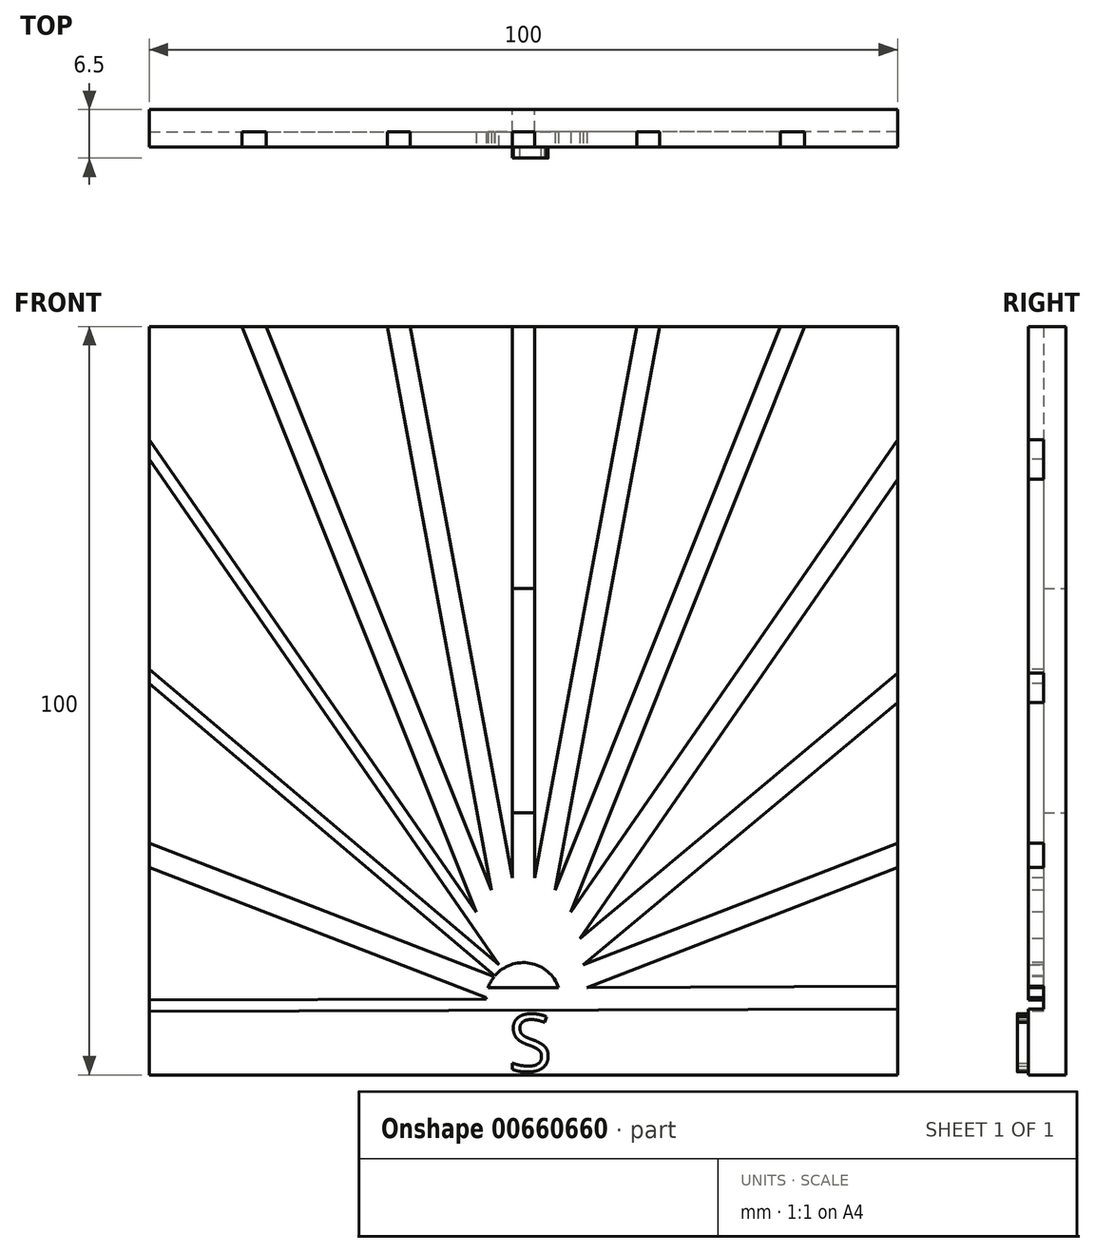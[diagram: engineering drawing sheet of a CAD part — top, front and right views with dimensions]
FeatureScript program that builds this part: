
annotation { "Feature Type Name" : "Feature", "Feature Type Description" : "" }
export const myFeature = defineFeature(function(context is Context, id is Id, definition is map)
    precondition{}
    {
        {
            var Q0;
            Q0=qCreatedBy(makeId("Front.planeOp"),FACE);
            var sketch = newSketch(context, id + "F0", { "sketchPlane" : qUnion([Q0])});
            skLineSegment(sketch, "E0.bottom", {"start": v(50, -50) * mm, "end": v(-50, -50) * mm});
            skLineSegment(sketch, "E0.top", {"start": v(50, 50) * mm, "end": v(-50, 50) * mm});
            skLineSegment(sketch, "E0.left", {"start": v(50, -50) * mm, "end": v(50, 50) * mm});
            skLineSegment(sketch, "E0.right", {"start": v(-50, -50) * mm, "end": v(-50, 50) * mm});
            skPoint(sketch, "E0.middle", {"position": v(0, 0) * mm});
            skLineSegment(sketch, "E1.bottom", {"start": v(1.5, -15) * mm, "end": v(-1.5, -15) * mm});
            skLineSegment(sketch, "E1.top", {"start": v(1.5, 15) * mm, "end": v(-1.5, 15) * mm});
            skLineSegment(sketch, "E1.left", {"start": v(1.5, -15) * mm, "end": v(1.5, 15) * mm});
            skLineSegment(sketch, "E1.right", {"start": v(-1.5, -15) * mm, "end": v(-1.5, 15) * mm});
            skSolve(sketch);
        }
        {
            var Q0;
            Q0=makeQuery(id+"F0.imprint","IMPRINT",FACE,{"disambiguationData":[TD([[makeQuery(id+"F0.imprint","IMPRINT",EDGE,{"derivedFrom":sQuery(id+"F0.wireOp",EDGE,"E0.bottom")}),-1.0]])]});
            extrude(context, id + "F1", {"entities" : qUnion([Q0]), "depth" : 5 * mm});
        }
        {
            var Q0;
            Q0=makeQuery(id+"F1.opExtrude","CAP_FACE",FACE,{"disambiguationData":[OSD([sQuery(id+"F0.wireOp",EDGE,"E0.bottom"),sQuery(id+"F0.wireOp",EDGE,"E0.top"),sQuery(id+"F0.wireOp",EDGE,"E0.left"),sQuery(id+"F0.wireOp",EDGE,"E0.right"),sQuery(id+"F0.wireOp",EDGE,"E1.bottom"),sQuery(id+"F0.wireOp",EDGE,"E1.top"),sQuery(id+"F0.wireOp",EDGE,"E1.left"),sQuery(id+"F0.wireOp",EDGE,"E1.right")])],"isStart":false});
            var sketch = newSketch(context, id + "F2", { "sketchPlane" : qUnion([Q0])});
            skPoint(sketch, "E2", {"position": v(0, -40) * mm});
            skLineSegment(sketch, "E3", {"start": v(-50, -40) * mm, "end": v(50, -40) * mm});
            skPoint(sketch, "E4", {"position": v(-50, -20.64) * mm});
            skLineSegment(sketch, "E5", {"start": v(0, -40) * mm, "end": v(-50, -20.64) * mm});
            skCircle(sketch, "E6", {"center": v(0, -40) * mm, "radius": 5 * mm});
            skPoint(sketch, "E7", {"position": v(-50, -19.03) * mm});
            skPoint(sketch, "E8", {"position": v(-50, -22.24) * mm});
            skLineSegment(sketch, "E9", {"start": v(-50, -22.24) * mm, "end": v(-4.99, -39.68) * mm});
            skLineSegment(sketch, "E10", {"start": v(-50, -19.03) * mm, "end": v(-3.9, -36.88) * mm});
            skSolve(sketch);
        }
        {
            var Q0;
            {var subQ5=sQuery(id+"F2.wireOp",EDGE,"E10");Q0=makeQuery(id+"F2.imprint","IMPRINT",FACE,{"disambiguationData":[TD([[makeQuery(id+"F2.imprint","IMPRINT",EDGE,{"derivedFrom":subQ5}),-1.0]])]});}
            var Q1;
            {var subQ5=sQuery(id+"F2.wireOp",EDGE,"E9");Q1=makeQuery(id+"F2.imprint","IMPRINT",FACE,{"disambiguationData":[TD([[makeQuery(id+"F2.imprint","IMPRINT",EDGE,{"derivedFrom":subQ5}),1.0]])]});}
            extrude(context, id + "F3", {"entities" : qUnion([Q0, Q1]), "operationType" : NewBodyOperationType.REMOVE, "oppositeDirection" : true, "depth" : 2 * mm});
        }
        {
            var Q0;
            Q0=makeQuery(id+"F1.opExtrude","CAP_FACE",FACE,{"disambiguationData":[OSD([sQuery(id+"F0.wireOp",EDGE,"E0.bottom"),sQuery(id+"F0.wireOp",EDGE,"E0.top"),sQuery(id+"F0.wireOp",EDGE,"E0.left"),sQuery(id+"F0.wireOp",EDGE,"E0.right"),sQuery(id+"F0.wireOp",EDGE,"E1.bottom"),sQuery(id+"F0.wireOp",EDGE,"E1.top"),sQuery(id+"F0.wireOp",EDGE,"E1.left"),sQuery(id+"F0.wireOp",EDGE,"E1.right")])],"isStart":false});
            var sketch = newSketch(context, id + "F4", { "sketchPlane" : qUnion([Q0])});
            skPoint(sketch, "E11", {"position": v(50, -41.82) * mm});
            skPoint(sketch, "E12", {"position": v(-50, 2.27) * mm});
            skPoint(sketch, "E13", {"position": v(0, -40) * mm});
            skCircle(sketch, "E14", {"center": v(0, -40) * mm, "radius": 5 * mm});
            skLineSegment(sketch, "E15", {"start": v(-50, 2.27) * mm, "end": v(0, -40) * mm});
            skLineSegment(sketch, "E16", {"start": v(0, -40) * mm, "end": v(-50, -39.68) * mm});
            skPoint(sketch, "E17", {"position": v(-50, 0.3) * mm});
            skPoint(sketch, "E18", {"position": v(-50, 4.23) * mm});
            skLineSegment(sketch, "E19", {"start": v(-50, 4.23) * mm, "end": v(-2.67, -35.78) * mm});
            skLineSegment(sketch, "E20", {"start": v(-50, 0.3) * mm, "end": v(-4.61, -38.07) * mm});
            skSolve(sketch);
        }
        {
            var Q0;
            {var subQ0=sQuery(id+"F4.wireOp",EDGE,"E19");Q0=makeQuery(id+"F4.imprint","IMPRINT",FACE,{"disambiguationData":[TD([[makeQuery(id+"F4.imprint","IMPRINT",EDGE,{"derivedFrom":subQ0}),-1.0]])]});}
            var Q1;
            {var subQ0=sQuery(id+"F4.wireOp",EDGE,"E14");var subQ1=sQuery(id+"F2.wireOp",EDGE,"E10");var subQ2=makeQuery(id+"F3.boolean.opBoolean","COPY",EDGE,{"derivedFrom":makeQuery(id+"F3.opExtrude","CAP_EDGE",EDGE,{"disambiguationData":[OSD([subQ1])],"isStart":true})});var subQ3=makeQuery(id+"F4.imprint","INTERSECT",VERTEX,{"derivedFrom":[subQ2,subQ0]});Q1=makeQuery(id+"F4.imprint","IMPRINT",FACE,{"disambiguationData":[TD([[makeQuery(id+"F4.imprint","IMPRINT",EDGE,{"disambiguationData":[TD([[subQ3,1.0]])],"derivedFrom":subQ0}),-1.0]])]});}
            extrude(context, id + "F5", {"entities" : qUnion([Q0, Q1]), "operationType" : NewBodyOperationType.REMOVE, "oppositeDirection" : true, "depth" : 2 * mm});
        }
        {
            var Q0;
            {var subQ0=sQuery(id+"F0.wireOp",EDGE,"E1.right");var subQ1=sQuery(id+"F0.wireOp",EDGE,"E1.left");var subQ2=sQuery(id+"F0.wireOp",EDGE,"E1.top");var subQ3=sQuery(id+"F0.wireOp",EDGE,"E1.bottom");var subQ4=sQuery(id+"F0.wireOp",EDGE,"E0.bottom");var subQ5=sQuery(id+"F0.wireOp",EDGE,"E0.right");var subQ6=sQuery(id+"F0.wireOp",EDGE,"E0.top");var subQ7=sQuery(id+"F0.wireOp",EDGE,"E0.left");Q0=makeQuery(id+"F5.boolean.opBoolean","SPLIT",FACE,{"disambiguationData":[TD([makeQuery(id+"F1.opExtrude","SWEPT_FACE",FACE,{"disambiguationData":[OSD([subQ4])]})])],"derivedFrom":makeQuery(id+"F1.opExtrude","CAP_FACE",FACE,{"disambiguationData":[OSD([subQ4,subQ6,subQ7,subQ5,subQ3,subQ2,subQ1,subQ0])],"isStart":false})});}
            var sketch = newSketch(context, id + "F6", { "sketchPlane" : qUnion([Q0])});
            skPoint(sketch, "E21", {"position": v(-50, 32.26) * mm});
            skPoint(sketch, "E22", {"position": v(0, -40) * mm});
            skCircle(sketch, "E23", {"center": v(0, -40) * mm, "radius": 5 * mm});
            skLineSegment(sketch, "E24", {"start": v(-50, 32.26) * mm, "end": v(0, -40) * mm});
            skLineSegment(sketch, "E25", {"start": v(0, -40) * mm, "end": v(-50, -40) * mm});
            skPoint(sketch, "E26", {"position": v(-50, 29.63) * mm});
            skPoint(sketch, "E27", {"position": v(-50, 34.9) * mm});
            skLineSegment(sketch, "E28", {"start": v(-50, 34.9) * mm, "end": v(-1.48, -35.22) * mm});
            skLineSegment(sketch, "E29", {"start": v(-50, 29.63) * mm, "end": v(-3.95, -36.93) * mm});
            skSolve(sketch);
        }
        {
            var Q0;
            {var subQ0=sQuery(id+"F6.wireOp",EDGE,"E28");Q0=makeQuery(id+"F6.imprint","IMPRINT",FACE,{"disambiguationData":[TD([[makeQuery(id+"F6.imprint","IMPRINT",EDGE,{"derivedFrom":subQ0}),-1.0]])]});}
            var Q1;
            {var subQ0=sQuery(id+"F6.wireOp",EDGE,"E23");var subQ1=sQuery(id+"F4.wireOp",EDGE,"E19");var subQ2=makeQuery(id+"F5.boolean.opBoolean","COPY",EDGE,{"derivedFrom":makeQuery(id+"F5.opExtrude","CAP_EDGE",EDGE,{"disambiguationData":[OSD([subQ1])],"isStart":true})});var subQ3=makeQuery(id+"F6.imprint","INTERSECT",VERTEX,{"derivedFrom":[subQ2,subQ0]});Q1=makeQuery(id+"F6.imprint","IMPRINT",FACE,{"disambiguationData":[TD([[makeQuery(id+"F6.imprint","IMPRINT",EDGE,{"disambiguationData":[TD([[subQ3,1.0]])],"derivedFrom":subQ0}),-1.0]])]});}
            var Q2;
            {var subQ6=sQuery(id+"F4.wireOp",EDGE,"E19");var subQ9=makeQuery(id+"F5.boolean.opBoolean","COPY",EDGE,{"derivedFrom":makeQuery(id+"F5.opExtrude","CAP_EDGE",EDGE,{"disambiguationData":[OSD([subQ6])],"isStart":true})});var subQ11=sQuery(id+"F6.wireOp",EDGE,"E29");var subQ12=makeQuery(id+"F6.imprint","INTERSECT",VERTEX,{"derivedFrom":[subQ9,subQ11]});Q2=makeQuery(id+"F6.imprint","IMPRINT",FACE,{"disambiguationData":[TD([[makeQuery(id+"F6.imprint","IMPRINT",EDGE,{"disambiguationData":[TD([[subQ12,-1.0]])],"derivedFrom":subQ9}),1.0]])]});}
            extrude(context, id + "F7", {"entities" : qUnion([Q0, Q1, Q2]), "operationType" : NewBodyOperationType.REMOVE, "oppositeDirection" : true, "depth" : 2 * mm});
        }
        {
            var Q0;
            {var subQ0=sQuery(id+"F0.wireOp",EDGE,"E1.right");var subQ2=sQuery(id+"F0.wireOp",EDGE,"E1.left");var subQ5=sQuery(id+"F0.wireOp",EDGE,"E1.top");var subQ7=sQuery(id+"F0.wireOp",EDGE,"E1.bottom");var subQ9=sQuery(id+"F0.wireOp",EDGE,"E0.bottom");var subQ10=makeQuery(id+"F1.opExtrude","SWEPT_FACE",FACE,{"disambiguationData":[OSD([subQ9])]});var subQ12=sQuery(id+"F0.wireOp",EDGE,"E0.right");var subQ14=sQuery(id+"F0.wireOp",EDGE,"E0.top");var subQ16=sQuery(id+"F0.wireOp",EDGE,"E0.left");Q0=makeQuery(id+"F7.boolean.opBoolean","SPLIT",FACE,{"disambiguationData":[TD([subQ10])],"derivedFrom":makeQuery(id+"F5.boolean.opBoolean","SPLIT",FACE,{"disambiguationData":[TD([subQ10])],"derivedFrom":makeQuery(id+"F1.opExtrude","CAP_FACE",FACE,{"disambiguationData":[OSD([subQ9,subQ14,subQ16,subQ12,subQ7,subQ5,subQ2,subQ0])],"isStart":false})})});}
            var sketch = newSketch(context, id + "F8", { "sketchPlane" : qUnion([Q0])});
            skPoint(sketch, "E30", {"position": v(0, -40) * mm});
            skPoint(sketch, "E31", {"position": v(-35.96, 50) * mm});
            skLineSegment(sketch, "E32", {"start": v(-35.96, 50) * mm, "end": v(0, -40) * mm});
            skLineSegment(sketch, "E33", {"start": v(0, -40) * mm, "end": v(-50, -40) * mm});
            skPoint(sketch, "E34", {"position": v(-37.58, 50) * mm});
            skPoint(sketch, "E35", {"position": v(-34.35, 50) * mm});
            skCircle(sketch, "E36", {"center": v(0, -40) * mm, "radius": 5 * mm});
            skLineSegment(sketch, "E37", {"start": v(-34.35, 50) * mm, "end": v(-0.38, -35.01) * mm});
            skLineSegment(sketch, "E38", {"start": v(-37.58, 50) * mm, "end": v(-3.16, -36.13) * mm});
            skSolve(sketch);
        }
        {
            var Q0;
            {var subQ0=sQuery(id+"F8.wireOp",EDGE,"E32");var subQ1=makeQuery(id+"F1.opExtrude","CAP_EDGE",EDGE,{"disambiguationData":[OSD([sQuery(id+"F0.wireOp",EDGE,"E0.top")])],"isStart":false});var subQ2=makeQuery(id+"F8.imprint","INTERSECT",VERTEX,{"derivedFrom":[subQ1,subQ0]});Q0=makeQuery(id+"F8.imprint","IMPRINT",FACE,{"disambiguationData":[TD([[makeQuery(id+"F8.imprint","IMPRINT",EDGE,{"disambiguationData":[TD([[subQ2,-1.0]])],"derivedFrom":subQ0}),-1.0]])]});}
            var Q1;
            {var subQ5=sQuery(id+"F8.wireOp",EDGE,"E37");Q1=makeQuery(id+"F8.imprint","IMPRINT",FACE,{"disambiguationData":[TD([[makeQuery(id+"F8.imprint","IMPRINT",EDGE,{"derivedFrom":subQ5}),-1.0]])]});}
            extrude(context, id + "F9", {"entities" : qUnion([Q0, Q1]), "operationType" : NewBodyOperationType.REMOVE, "oppositeDirection" : true, "depth" : 2 * mm});
        }
        {
            var Q0;
            {var subQ0=sQuery(id+"F0.wireOp",EDGE,"E1.right");var subQ2=sQuery(id+"F0.wireOp",EDGE,"E1.left");var subQ5=sQuery(id+"F0.wireOp",EDGE,"E1.top");var subQ8=sQuery(id+"F0.wireOp",EDGE,"E1.bottom");var subQ10=sQuery(id+"F0.wireOp",EDGE,"E0.bottom");var subQ11=makeQuery(id+"F1.opExtrude","SWEPT_FACE",FACE,{"disambiguationData":[OSD([subQ10])]});var subQ13=sQuery(id+"F0.wireOp",EDGE,"E0.right");var subQ15=sQuery(id+"F0.wireOp",EDGE,"E0.top");var subQ17=sQuery(id+"F0.wireOp",EDGE,"E0.left");Q0=makeQuery(id+"F9.boolean.opBoolean","SPLIT",FACE,{"disambiguationData":[TD([subQ11])],"derivedFrom":makeQuery(id+"F7.boolean.opBoolean","SPLIT",FACE,{"disambiguationData":[TD([subQ11])],"derivedFrom":makeQuery(id+"F5.boolean.opBoolean","SPLIT",FACE,{"disambiguationData":[TD([subQ11])],"derivedFrom":makeQuery(id+"F1.opExtrude","CAP_FACE",FACE,{"disambiguationData":[OSD([subQ10,subQ15,subQ17,subQ13,subQ8,subQ5,subQ2,subQ0])],"isStart":false})})})});}
            var sketch = newSketch(context, id + "F10", { "sketchPlane" : qUnion([Q0])});
            skPoint(sketch, "E39", {"position": v(0, -40) * mm});
            skPoint(sketch, "E40", {"position": v(-16.68, 50) * mm});
            skPoint(sketch, "E41", {"position": v(-15.15, 50) * mm});
            skPoint(sketch, "E42", {"position": v(-18.2, 50) * mm});
            skCircle(sketch, "E43", {"center": v(0, -40) * mm, "radius": 5 * mm});
            skLineSegment(sketch, "E44", {"start": v(-16.68, 50) * mm, "end": v(0, -40) * mm});
            skLineSegment(sketch, "E45", {"start": v(0, -40) * mm, "end": v(-50, -40) * mm});
            skLineSegment(sketch, "E46", {"start": v(-18.2, 50) * mm, "end": v(-2.34, -35.58) * mm});
            skLineSegment(sketch, "E47", {"start": v(-15.15, 50) * mm, "end": v(0.6, -35.04) * mm});
            skSolve(sketch);
        }
        {
            var Q0;
            {var subQ3=sQuery(id+"F8.wireOp",EDGE,"E37");var subQ6=makeQuery(id+"F9.boolean.opBoolean","COPY",EDGE,{"derivedFrom":makeQuery(id+"F9.opExtrude","CAP_EDGE",EDGE,{"disambiguationData":[OSD([subQ3])],"isStart":true})});var subQ8=sQuery(id+"F10.wireOp",EDGE,"E46");var subQ10=makeQuery(id+"F10.imprint","INTERSECT",VERTEX,{"derivedFrom":[subQ6,subQ8]});Q0=makeQuery(id+"F10.imprint","IMPRINT",FACE,{"disambiguationData":[TD([[makeQuery(id+"F10.imprint","IMPRINT",EDGE,{"disambiguationData":[TD([[subQ10,-1.0]])],"derivedFrom":subQ6}),1.0]])]});}
            var Q1;
            {var subQ6=sQuery(id+"F10.wireOp",EDGE,"E47");Q1=makeQuery(id+"F10.imprint","IMPRINT",FACE,{"disambiguationData":[TD([[makeQuery(id+"F10.imprint","IMPRINT",EDGE,{"derivedFrom":subQ6}),-1.0]])]});}
            extrude(context, id + "F11", {"entities" : qUnion([Q0, Q1]), "operationType" : NewBodyOperationType.REMOVE, "oppositeDirection" : true, "depth" : 2 * mm});
        }
        {
            var Q0;
            {var subQ0=sQuery(id+"F0.wireOp",EDGE,"E1.right");var subQ2=sQuery(id+"F0.wireOp",EDGE,"E1.left");var subQ5=sQuery(id+"F0.wireOp",EDGE,"E1.top");var subQ8=sQuery(id+"F0.wireOp",EDGE,"E1.bottom");var subQ10=sQuery(id+"F0.wireOp",EDGE,"E0.bottom");var subQ11=makeQuery(id+"F1.opExtrude","SWEPT_FACE",FACE,{"disambiguationData":[OSD([subQ10])]});var subQ13=sQuery(id+"F0.wireOp",EDGE,"E0.right");var subQ15=sQuery(id+"F0.wireOp",EDGE,"E0.top");var subQ17=sQuery(id+"F0.wireOp",EDGE,"E0.left");Q0=makeQuery(id+"F11.boolean.opBoolean","SPLIT",FACE,{"disambiguationData":[TD([subQ11])],"derivedFrom":makeQuery(id+"F9.boolean.opBoolean","SPLIT",FACE,{"disambiguationData":[TD([subQ11])],"derivedFrom":makeQuery(id+"F7.boolean.opBoolean","SPLIT",FACE,{"disambiguationData":[TD([subQ11])],"derivedFrom":makeQuery(id+"F5.boolean.opBoolean","SPLIT",FACE,{"disambiguationData":[TD([subQ11])],"derivedFrom":makeQuery(id+"F1.opExtrude","CAP_FACE",FACE,{"disambiguationData":[OSD([subQ10,subQ15,subQ17,subQ13,subQ8,subQ5,subQ2,subQ0])],"isStart":false})})})})});}
            var sketch = newSketch(context, id + "F12", { "sketchPlane" : qUnion([Q0])});
            skPoint(sketch, "E48", {"position": v(0, -40) * mm});
            skPoint(sketch, "E49", {"position": v(0, 50) * mm});
            skLineSegment(sketch, "E50", {"start": v(0, 50) * mm, "end": v(0, -40) * mm});
            skPoint(sketch, "E51", {"position": v(-1.5, 50) * mm});
            skPoint(sketch, "E52", {"position": v(1.5, 50) * mm});
            skCircle(sketch, "E53", {"center": v(0, -40) * mm, "radius": 5 * mm});
            skLineSegment(sketch, "E54", {"start": v(-1.5, 50) * mm, "end": v(-1.5, -35.23) * mm});
            skLineSegment(sketch, "E55", {"start": v(1.5, 50) * mm, "end": v(1.5, -35.23) * mm});
            skSolve(sketch);
        }
        {
            var Q0;
            {var subQ0=sQuery(id+"F12.wireOp",EDGE,"E50");var subQ1=sQuery(id+"F0.wireOp",EDGE,"E1.top");var subQ9=makeQuery(id+"F1.opExtrude","CAP_EDGE",EDGE,{"disambiguationData":[OSD([subQ1])],"isStart":false});var subQ10=makeQuery(id+"F12.imprint","INTERSECT",VERTEX,{"derivedFrom":[subQ9,subQ0]});Q0=makeQuery(id+"F12.imprint","IMPRINT",FACE,{"disambiguationData":[TD([[makeQuery(id+"F12.imprint","IMPRINT",EDGE,{"disambiguationData":[TD([[subQ10,-1.0]])],"derivedFrom":subQ9}),-1.0]])]});}
            var Q1;
            {var subQ0=sQuery(id+"F12.wireOp",EDGE,"E50");var subQ1=sQuery(id+"F0.wireOp",EDGE,"E1.top");var subQ9=makeQuery(id+"F1.opExtrude","CAP_EDGE",EDGE,{"disambiguationData":[OSD([subQ1])],"isStart":false});var subQ10=makeQuery(id+"F12.imprint","INTERSECT",VERTEX,{"derivedFrom":[subQ9,subQ0]});Q1=makeQuery(id+"F12.imprint","IMPRINT",FACE,{"disambiguationData":[TD([[makeQuery(id+"F12.imprint","IMPRINT",EDGE,{"disambiguationData":[TD([[subQ10,1.0]])],"derivedFrom":subQ9}),-1.0]])]});}
            var Q2;
            {var subQ0=sQuery(id+"F12.wireOp",EDGE,"E50");var subQ1=makeQuery(id+"F1.opExtrude","CAP_EDGE",EDGE,{"disambiguationData":[OSD([sQuery(id+"F0.wireOp",EDGE,"E1.bottom")])],"isStart":false});var subQ2=makeQuery(id+"F12.imprint","INTERSECT",VERTEX,{"derivedFrom":[subQ1,subQ0]});Q2=makeQuery(id+"F12.imprint","IMPRINT",FACE,{"disambiguationData":[TD([[makeQuery(id+"F12.imprint","IMPRINT",EDGE,{"disambiguationData":[TD([[subQ2,-1.0]])],"derivedFrom":subQ0}),-1.0]])]});}
            var Q3;
            {var subQ3=makeQuery(id+"F1.opExtrude","CAP_EDGE",EDGE,{"disambiguationData":[OSD([sQuery(id+"F0.wireOp",EDGE,"E1.bottom")])],"isStart":false});var subQ7=sQuery(id+"F12.wireOp",EDGE,"E50");var subQ9=makeQuery(id+"F12.imprint","INTERSECT",VERTEX,{"derivedFrom":[subQ3,subQ7]});Q3=makeQuery(id+"F12.imprint","IMPRINT",FACE,{"disambiguationData":[TD([[makeQuery(id+"F12.imprint","IMPRINT",EDGE,{"disambiguationData":[TD([[subQ9,-1.0]])],"derivedFrom":subQ7}),1.0]])]});}
            var Q4;
            {var subQ0=sQuery(id+"F12.wireOp",EDGE,"E53");var subQ1=sQuery(id+"F12.wireOp",EDGE,"E50");var subQ2=makeQuery(id+"F12.imprint","INTERSECT",VERTEX,{"derivedFrom":[subQ1,subQ0]});Q4=makeQuery(id+"F12.imprint","IMPRINT",FACE,{"disambiguationData":[TD([[makeQuery(id+"F12.imprint","IMPRINT",EDGE,{"disambiguationData":[TD([[subQ2,1.0]])],"derivedFrom":subQ1}),-1.0]])]});}
            extrude(context, id + "F13", {"entities" : qUnion([Q0, Q1, Q2, Q3, Q4]), "operationType" : NewBodyOperationType.REMOVE, "oppositeDirection" : true, "depth" : 2 * mm});
        }
        {
            var Q0;
            {var subQ0=sQuery(id+"F0.wireOp",EDGE,"E1.left");var subQ3=sQuery(id+"F0.wireOp",EDGE,"E1.top");var subQ7=sQuery(id+"F0.wireOp",EDGE,"E1.bottom");var subQ9=sQuery(id+"F0.wireOp",EDGE,"E0.bottom");var subQ10=makeQuery(id+"F1.opExtrude","SWEPT_FACE",FACE,{"disambiguationData":[OSD([subQ9])]});var subQ12=sQuery(id+"F0.wireOp",EDGE,"E0.right");var subQ14=sQuery(id+"F0.wireOp",EDGE,"E0.top");var subQ20=sQuery(id+"F0.wireOp",EDGE,"E0.left");var subQ24=sQuery(id+"F0.wireOp",EDGE,"E1.right");var subQ25=makeQuery(id+"F1.opExtrude","CAP_FACE",FACE,{"disambiguationData":[OSD([subQ9,subQ14,subQ20,subQ12,subQ7,subQ3,subQ0,subQ24])],"isStart":false});Q0=makeQuery(id+"F13.boolean.opBoolean","SPLIT",FACE,{"disambiguationData":[TD([subQ10])],"derivedFrom":makeQuery(id+"F11.boolean.opBoolean","SPLIT",FACE,{"disambiguationData":[TD([subQ10])],"derivedFrom":makeQuery(id+"F9.boolean.opBoolean","SPLIT",FACE,{"disambiguationData":[TD([subQ10])],"derivedFrom":makeQuery(id+"F7.boolean.opBoolean","SPLIT",FACE,{"disambiguationData":[TD([subQ10])],"derivedFrom":makeQuery(id+"F5.boolean.opBoolean","SPLIT",FACE,{"disambiguationData":[TD([subQ10])],"derivedFrom":subQ25})})})})});}
            var sketch = newSketch(context, id + "F14", { "sketchPlane" : qUnion([Q0])});
            skPoint(sketch, "E56", {"position": v(16.68, 50) * mm});
            skPoint(sketch, "E57", {"position": v(0, -40) * mm});
            skCircle(sketch, "E58", {"center": v(0, -40) * mm, "radius": 5 * mm});
            skLineSegment(sketch, "E59", {"start": v(16.68, 50) * mm, "end": v(0, -40) * mm});
            skLineSegment(sketch, "E60", {"start": v(0, -40) * mm, "end": v(50, -40) * mm});
            skPoint(sketch, "E61", {"position": v(15.15, 50) * mm});
            skPoint(sketch, "E62", {"position": v(18.2, 50) * mm});
            skLineSegment(sketch, "E63", {"start": v(18.2, 50) * mm, "end": v(2.34, -35.58) * mm});
            skLineSegment(sketch, "E64", {"start": v(15.15, 50) * mm, "end": v(-0.6, -35.04) * mm});
            skSolve(sketch);
        }
        {
            var Q0;
            {var subQ7=sQuery(id+"F14.wireOp",EDGE,"E63");Q0=makeQuery(id+"F14.imprint","IMPRINT",FACE,{"disambiguationData":[TD([[makeQuery(id+"F14.imprint","IMPRINT",EDGE,{"derivedFrom":subQ7}),-1.0]])]});}
            var Q1;
            {var subQ6=sQuery(id+"F12.wireOp",EDGE,"E55");var subQ12=makeQuery(id+"F13.boolean.opBoolean","COPY",EDGE,{"derivedFrom":makeQuery(id+"F13.opExtrude","CAP_EDGE",EDGE,{"disambiguationData":[OSD([subQ6]),TDD([makeQuery(id+"F12.imprint","IMPRINT",EDGE,{"disambiguationData":[TD([[makeQuery(id+"F12.imprint","INTERSECT",VERTEX,{"derivedFrom":[sQuery(id+"F12.wireOp",EDGE,"E53"),subQ6]}),1.0]])],"derivedFrom":subQ6})])],"isStart":true})});var subQ14=sQuery(id+"F14.wireOp",EDGE,"U3o0jyPI-7KGk-aDnc-HRvP-a0akFUZvhtuf");var subQ16=makeQuery(id+"F14.imprint","INTERSECT",VERTEX,{"derivedFrom":[subQ12,subQ14]});Q1=makeQuery(id+"F14.imprint","IMPRINT",FACE,{"disambiguationData":[TD([[makeQuery(id+"F14.imprint","IMPRINT",EDGE,{"disambiguationData":[TD([[subQ16,-1.0]])],"derivedFrom":subQ12}),1.0]])]});}
            var Q2;
            {var subQ1=sQuery(id+"F0.wireOp",EDGE,"E0.left");var subQ2=makeQuery(id+"F1.opExtrude","SWEPT_FACE",FACE,{"disambiguationData":[OSD([subQ1])]});var subQ3=sQuery(id+"F0.wireOp",EDGE,"E1.left");var subQ4=sQuery(id+"F0.wireOp",EDGE,"E0.top");var subQ6=sQuery(id+"F12.wireOp",EDGE,"E55");var subQ7=sQuery(id+"F0.wireOp",EDGE,"E1.bottom");var subQ8=makeQuery(id+"F12.imprint","IMPRINT",EDGE,{"disambiguationData":[TD([[makeQuery(id+"F12.imprint","INTERSECT",VERTEX,{"derivedFrom":[makeQuery(id+"F1.opExtrude","CAP_EDGE",EDGE,{"disambiguationData":[OSD([subQ7])],"isStart":false}),subQ6]}),-1.0],[makeQuery(id+"F12.imprint","INTERSECT",VERTEX,{"derivedFrom":[sQuery(id+"F12.wireOp",EDGE,"E53"),subQ6]}),1.0]])],"derivedFrom":subQ6});var subQ9=sQuery(id+"F0.wireOp",EDGE,"E1.top");var subQ11=makeQuery(id+"F11.boolean.opBoolean","SPLIT",EDGE,{"disambiguationData":[TD([subQ2])],"derivedFrom":makeQuery(id+"F9.boolean.opBoolean","SPLIT",EDGE,{"disambiguationData":[TD([subQ2])],"derivedFrom":makeQuery(id+"F1.opExtrude","CAP_EDGE",EDGE,{"disambiguationData":[OSD([subQ4])],"isStart":false})})});var subQ12=makeQuery(id+"F12.imprint","IMPRINT",EDGE,{"disambiguationData":[TD([[makeQuery(id+"F12.imprint","INTERSECT",VERTEX,{"derivedFrom":[makeQuery(id+"F1.opExtrude","CAP_EDGE",EDGE,{"disambiguationData":[OSD([subQ9])],"isStart":false}),subQ6]}),1.0],[makeQuery(id+"F12.imprint","INTERSECT",VERTEX,{"derivedFrom":[subQ11,subQ6]}),-1.0]])],"derivedFrom":subQ6});var subQ15=makeQuery(id+"F13.boolean.opBoolean","MERGE",EDGE,{"derivedFrom":[makeQuery(id+"F1.opExtrude","CAP_EDGE",EDGE,{"disambiguationData":[OSD([subQ3])],"isStart":false}),makeQuery(id+"F13.opExtrude","CAP_EDGE",EDGE,{"disambiguationData":[OSD([subQ6]),TDD([subQ12])],"isStart":true}),makeQuery(id+"F13.opExtrude","CAP_EDGE",EDGE,{"disambiguationData":[OSD([subQ6]),TDD([subQ8])],"isStart":true})]});var subQ17=sQuery(id+"F14.wireOp",EDGE,"E64");var subQ18=makeQuery(id+"F14.imprint","INTERSECT",VERTEX,{"derivedFrom":[subQ15,subQ17]});Q2=makeQuery(id+"F14.imprint","IMPRINT",FACE,{"disambiguationData":[TD([[makeQuery(id+"F14.imprint","IMPRINT",EDGE,{"disambiguationData":[TD([[subQ18,1.0]])],"derivedFrom":subQ15}),-1.0]])]});}
            extrude(context, id + "F15", {"entities" : qUnion([Q0, Q1, Q2]), "operationType" : NewBodyOperationType.REMOVE, "oppositeDirection" : true, "depth" : 2 * mm});
        }
        {
            var Q0;
            {var subQ4=sQuery(id+"F0.wireOp",EDGE,"E0.bottom");var subQ5=makeQuery(id+"F1.opExtrude","SWEPT_FACE",FACE,{"disambiguationData":[OSD([subQ4])]});var subQ8=sQuery(id+"F0.wireOp",EDGE,"E0.right");var subQ10=sQuery(id+"F0.wireOp",EDGE,"E0.top");var subQ17=sQuery(id+"F0.wireOp",EDGE,"E0.left");var subQ19=sQuery(id+"F0.wireOp",EDGE,"E1.left");var subQ21=sQuery(id+"F0.wireOp",EDGE,"E1.top");var subQ23=sQuery(id+"F0.wireOp",EDGE,"E1.bottom");var subQ25=sQuery(id+"F0.wireOp",EDGE,"E1.right");var subQ26=makeQuery(id+"F1.opExtrude","CAP_FACE",FACE,{"disambiguationData":[OSD([subQ4,subQ10,subQ17,subQ8,subQ23,subQ21,subQ19,subQ25])],"isStart":false});Q0=makeQuery(id+"F15.boolean.opBoolean","SPLIT",FACE,{"disambiguationData":[TD([subQ5])],"derivedFrom":makeQuery(id+"F13.boolean.opBoolean","SPLIT",FACE,{"disambiguationData":[TD([subQ5])],"derivedFrom":makeQuery(id+"F11.boolean.opBoolean","SPLIT",FACE,{"disambiguationData":[TD([subQ5])],"derivedFrom":makeQuery(id+"F9.boolean.opBoolean","SPLIT",FACE,{"disambiguationData":[TD([subQ5])],"derivedFrom":makeQuery(id+"F7.boolean.opBoolean","SPLIT",FACE,{"disambiguationData":[TD([subQ5])],"derivedFrom":makeQuery(id+"F5.boolean.opBoolean","SPLIT",FACE,{"disambiguationData":[TD([subQ5])],"derivedFrom":subQ26})})})})})});}
            var sketch = newSketch(context, id + "F16", { "sketchPlane" : qUnion([Q0])});
            skPoint(sketch, "E65", {"position": v(35.96, 50) * mm});
            skPoint(sketch, "E66", {"position": v(0, -40) * mm});
            skPoint(sketch, "E67", {"position": v(34.35, 50) * mm});
            skPoint(sketch, "E68", {"position": v(37.58, 50) * mm});
            skCircle(sketch, "E69", {"center": v(0, -40) * mm, "radius": 5 * mm});
            skLineSegment(sketch, "E70", {"start": v(35.96, 50) * mm, "end": v(0, -40) * mm});
            skLineSegment(sketch, "E71", {"start": v(0, -40) * mm, "end": v(50, -40) * mm});
            skLineSegment(sketch, "E72", {"start": v(37.58, 50) * mm, "end": v(3.16, -36.13) * mm});
            skLineSegment(sketch, "E73", {"start": v(34.35, 50) * mm, "end": v(0.38, -35.01) * mm});
            skSolve(sketch);
        }
        {
            var Q0;
            {var subQ7=sQuery(id+"F14.wireOp",EDGE,"E63");var subQ12=makeQuery(id+"F15.boolean.opBoolean","COPY",EDGE,{"derivedFrom":makeQuery(id+"F15.opExtrude","CAP_EDGE",EDGE,{"disambiguationData":[OSD([subQ7])],"isStart":true})});var subQ14=sQuery(id+"F16.wireOp",EDGE,"E73");var subQ15=makeQuery(id+"F16.imprint","INTERSECT",VERTEX,{"derivedFrom":[subQ12,subQ14]});Q0=makeQuery(id+"F16.imprint","IMPRINT",FACE,{"disambiguationData":[TD([[makeQuery(id+"F16.imprint","IMPRINT",EDGE,{"disambiguationData":[TD([[subQ15,-1.0]])],"derivedFrom":subQ12}),1.0]])]});}
            var Q1;
            {var subQ6=sQuery(id+"F16.wireOp",EDGE,"E72");Q1=makeQuery(id+"F16.imprint","IMPRINT",FACE,{"disambiguationData":[TD([[makeQuery(id+"F16.imprint","IMPRINT",EDGE,{"derivedFrom":subQ6}),-1.0]])]});}
            extrude(context, id + "F17", {"entities" : qUnion([Q0, Q1]), "operationType" : NewBodyOperationType.REMOVE, "oppositeDirection" : true, "depth" : 2 * mm});
        }
        {
            var Q0;
            {var subQ4=sQuery(id+"F0.wireOp",EDGE,"E0.bottom");var subQ5=makeQuery(id+"F1.opExtrude","SWEPT_FACE",FACE,{"disambiguationData":[OSD([subQ4])]});var subQ9=sQuery(id+"F0.wireOp",EDGE,"E0.right");var subQ11=sQuery(id+"F0.wireOp",EDGE,"E0.top");var subQ18=sQuery(id+"F0.wireOp",EDGE,"E0.left");var subQ20=sQuery(id+"F0.wireOp",EDGE,"E1.left");var subQ22=sQuery(id+"F0.wireOp",EDGE,"E1.bottom");var subQ23=sQuery(id+"F0.wireOp",EDGE,"E1.top");var subQ24=sQuery(id+"F0.wireOp",EDGE,"E1.right");var subQ25=makeQuery(id+"F1.opExtrude","CAP_FACE",FACE,{"disambiguationData":[OSD([subQ4,subQ11,subQ18,subQ9,subQ22,subQ23,subQ20,subQ24])],"isStart":false});Q0=makeQuery(id+"F17.boolean.opBoolean","SPLIT",FACE,{"disambiguationData":[TD([subQ5])],"derivedFrom":makeQuery(id+"F15.boolean.opBoolean","SPLIT",FACE,{"disambiguationData":[TD([subQ5])],"derivedFrom":makeQuery(id+"F13.boolean.opBoolean","SPLIT",FACE,{"disambiguationData":[TD([subQ5])],"derivedFrom":makeQuery(id+"F11.boolean.opBoolean","SPLIT",FACE,{"disambiguationData":[TD([subQ5])],"derivedFrom":makeQuery(id+"F9.boolean.opBoolean","SPLIT",FACE,{"disambiguationData":[TD([subQ5])],"derivedFrom":makeQuery(id+"F7.boolean.opBoolean","SPLIT",FACE,{"disambiguationData":[TD([subQ5])],"derivedFrom":makeQuery(id+"F5.boolean.opBoolean","SPLIT",FACE,{"disambiguationData":[TD([subQ5])],"derivedFrom":subQ25})})})})})})});}
            var sketch = newSketch(context, id + "F18", { "sketchPlane" : qUnion([Q0])});
            skPoint(sketch, "E74", {"position": v(50, 32.26) * mm});
            skPoint(sketch, "E75", {"position": v(50, 34.9) * mm});
            skPoint(sketch, "E76", {"position": v(50, 29.63) * mm});
            skPoint(sketch, "E77", {"position": v(0, -40) * mm});
            skLineSegment(sketch, "E78", {"start": v(50, 32.26) * mm, "end": v(0, -40) * mm});
            skLineSegment(sketch, "E79", {"start": v(0, -40) * mm, "end": v(50, -40) * mm});
            skCircle(sketch, "E80", {"center": v(0, -40) * mm, "radius": 5 * mm});
            skLineSegment(sketch, "E81", {"start": v(50, 34.9) * mm, "end": v(1.48, -35.22) * mm});
            skLineSegment(sketch, "E82", {"start": v(50, 29.63) * mm, "end": v(3.95, -36.93) * mm});
            skSolve(sketch);
        }
        {
            var Q0;
            {var subQ0=sQuery(id+"F18.wireOp",EDGE,"E78");var subQ1=makeQuery(id+"F1.opExtrude","CAP_EDGE",EDGE,{"disambiguationData":[OSD([sQuery(id+"F0.wireOp",EDGE,"E0.left")])],"isStart":false});var subQ2=makeQuery(id+"F18.imprint","INTERSECT",VERTEX,{"derivedFrom":[subQ1,subQ0]});Q0=makeQuery(id+"F18.imprint","IMPRINT",FACE,{"disambiguationData":[TD([[makeQuery(id+"F18.imprint","IMPRINT",EDGE,{"disambiguationData":[TD([[subQ2,-1.0]])],"derivedFrom":subQ0}),-1.0]])]});}
            var Q1;
            {var subQ0=sQuery(id+"F18.wireOp",EDGE,"E82");Q1=makeQuery(id+"F18.imprint","IMPRINT",FACE,{"disambiguationData":[TD([[makeQuery(id+"F18.imprint","IMPRINT",EDGE,{"derivedFrom":subQ0}),-1.0]])]});}
            extrude(context, id + "F19", {"entities" : qUnion([Q0, Q1]), "operationType" : NewBodyOperationType.REMOVE, "oppositeDirection" : true, "depth" : 2 * mm});
        }
        {
            var Q0;
            {var subQ10=sQuery(id+"F0.wireOp",EDGE,"E0.bottom");var subQ11=makeQuery(id+"F1.opExtrude","SWEPT_FACE",FACE,{"disambiguationData":[OSD([subQ10])]});var subQ12=sQuery(id+"F0.wireOp",EDGE,"E0.left");var subQ15=sQuery(id+"F0.wireOp",EDGE,"E0.right");var subQ19=sQuery(id+"F0.wireOp",EDGE,"E0.top");var subQ21=sQuery(id+"F0.wireOp",EDGE,"E1.left");var subQ23=sQuery(id+"F0.wireOp",EDGE,"E1.bottom");var subQ24=sQuery(id+"F0.wireOp",EDGE,"E1.top");var subQ25=sQuery(id+"F0.wireOp",EDGE,"E1.right");var subQ26=makeQuery(id+"F1.opExtrude","CAP_FACE",FACE,{"disambiguationData":[OSD([subQ10,subQ19,subQ12,subQ15,subQ23,subQ24,subQ21,subQ25])],"isStart":false});Q0=makeQuery(id+"F19.boolean.opBoolean","SPLIT",FACE,{"disambiguationData":[TD([subQ11])],"derivedFrom":makeQuery(id+"F17.boolean.opBoolean","SPLIT",FACE,{"disambiguationData":[TD([subQ11])],"derivedFrom":makeQuery(id+"F15.boolean.opBoolean","SPLIT",FACE,{"disambiguationData":[TD([subQ11])],"derivedFrom":makeQuery(id+"F13.boolean.opBoolean","SPLIT",FACE,{"disambiguationData":[TD([subQ11])],"derivedFrom":makeQuery(id+"F11.boolean.opBoolean","SPLIT",FACE,{"disambiguationData":[TD([subQ11])],"derivedFrom":makeQuery(id+"F9.boolean.opBoolean","SPLIT",FACE,{"disambiguationData":[TD([subQ11])],"derivedFrom":makeQuery(id+"F7.boolean.opBoolean","SPLIT",FACE,{"disambiguationData":[TD([subQ11])],"derivedFrom":makeQuery(id+"F5.boolean.opBoolean","SPLIT",FACE,{"disambiguationData":[TD([subQ11])],"derivedFrom":subQ26})})})})})})})});}
            var sketch = newSketch(context, id + "F20", { "sketchPlane" : qUnion([Q0])});
            skPoint(sketch, "E83", {"position": v(50, 1.72) * mm});
            skPoint(sketch, "E84", {"position": v(50, 3.67) * mm});
            skPoint(sketch, "E85", {"position": v(0, -40) * mm});
            skLineSegment(sketch, "E86", {"start": v(50, 1.72) * mm, "end": v(0, -40) * mm});
            skLineSegment(sketch, "E87", {"start": v(0, -40) * mm, "end": v(50, -40) * mm});
            skPoint(sketch, "E88", {"position": v(50, -0.24) * mm});
            skCircle(sketch, "E89", {"center": v(0, -40) * mm, "radius": 5 * mm});
            skLineSegment(sketch, "E90", {"start": v(50, 3.67) * mm, "end": v(2.7, -35.8) * mm});
            skLineSegment(sketch, "E91", {"start": v(50, -0.24) * mm, "end": v(4.62, -38.1) * mm});
            skSolve(sketch);
        }
        {
            var Q0;
            {var subQ3=sQuery(id+"F18.wireOp",EDGE,"E82");var subQ6=makeQuery(id+"F19.boolean.opBoolean","COPY",EDGE,{"derivedFrom":makeQuery(id+"F19.opExtrude","CAP_EDGE",EDGE,{"disambiguationData":[OSD([subQ3])],"isStart":true})});var subQ8=sQuery(id+"F20.wireOp",EDGE,"E90");var subQ10=makeQuery(id+"F20.imprint","INTERSECT",VERTEX,{"derivedFrom":[subQ6,subQ8]});Q0=makeQuery(id+"F20.imprint","IMPRINT",FACE,{"disambiguationData":[TD([[makeQuery(id+"F20.imprint","IMPRINT",EDGE,{"disambiguationData":[TD([[subQ10,-1.0]])],"derivedFrom":subQ6}),1.0]])]});}
            var Q1;
            {var subQ6=sQuery(id+"F20.wireOp",EDGE,"E91");Q1=makeQuery(id+"F20.imprint","IMPRINT",FACE,{"disambiguationData":[TD([[makeQuery(id+"F20.imprint","IMPRINT",EDGE,{"derivedFrom":subQ6}),-1.0]])]});}
            extrude(context, id + "F21", {"entities" : qUnion([Q0, Q1]), "operationType" : NewBodyOperationType.REMOVE, "oppositeDirection" : true, "depth" : 2 * mm});
        }
        {
            var Q0;
            {var subQ10=sQuery(id+"F0.wireOp",EDGE,"E0.bottom");var subQ11=makeQuery(id+"F1.opExtrude","SWEPT_FACE",FACE,{"disambiguationData":[OSD([subQ10])]});var subQ12=sQuery(id+"F0.wireOp",EDGE,"E0.left");var subQ15=sQuery(id+"F0.wireOp",EDGE,"E0.right");var subQ20=sQuery(id+"F0.wireOp",EDGE,"E0.top");var subQ22=sQuery(id+"F0.wireOp",EDGE,"E1.left");var subQ24=sQuery(id+"F0.wireOp",EDGE,"E1.bottom");var subQ25=sQuery(id+"F0.wireOp",EDGE,"E1.top");var subQ26=sQuery(id+"F0.wireOp",EDGE,"E1.right");var subQ27=makeQuery(id+"F1.opExtrude","CAP_FACE",FACE,{"disambiguationData":[OSD([subQ10,subQ20,subQ12,subQ15,subQ24,subQ25,subQ22,subQ26])],"isStart":false});Q0=makeQuery(id+"F21.boolean.opBoolean","SPLIT",FACE,{"disambiguationData":[TD([subQ11])],"derivedFrom":makeQuery(id+"F19.boolean.opBoolean","SPLIT",FACE,{"disambiguationData":[TD([subQ11])],"derivedFrom":makeQuery(id+"F17.boolean.opBoolean","SPLIT",FACE,{"disambiguationData":[TD([subQ11])],"derivedFrom":makeQuery(id+"F15.boolean.opBoolean","SPLIT",FACE,{"disambiguationData":[TD([subQ11])],"derivedFrom":makeQuery(id+"F13.boolean.opBoolean","SPLIT",FACE,{"disambiguationData":[TD([subQ11])],"derivedFrom":makeQuery(id+"F11.boolean.opBoolean","SPLIT",FACE,{"disambiguationData":[TD([subQ11])],"derivedFrom":makeQuery(id+"F9.boolean.opBoolean","SPLIT",FACE,{"disambiguationData":[TD([subQ11])],"derivedFrom":makeQuery(id+"F7.boolean.opBoolean","SPLIT",FACE,{"disambiguationData":[TD([subQ11])],"derivedFrom":makeQuery(id+"F5.boolean.opBoolean","SPLIT",FACE,{"disambiguationData":[TD([subQ11])],"derivedFrom":subQ27})})})})})})})})});}
            var sketch = newSketch(context, id + "F22", { "sketchPlane" : qUnion([Q0])});
            skPoint(sketch, "E92", {"position": v(50, -20.64) * mm});
            skPoint(sketch, "E93", {"position": v(50, -19.03) * mm});
            skPoint(sketch, "E94", {"position": v(50, -22.24) * mm});
            skPoint(sketch, "E95", {"position": v(0, -40) * mm});
            skLineSegment(sketch, "E96", {"start": v(50, -20.64) * mm, "end": v(0, -40) * mm});
            skCircle(sketch, "E97", {"center": v(0, -40) * mm, "radius": 5 * mm});
            skLineSegment(sketch, "E98", {"start": v(50, -19.03) * mm, "end": v(3.9, -36.88) * mm});
            skLineSegment(sketch, "E99", {"start": v(50, -22.24) * mm, "end": v(4.99, -39.68) * mm});
            skLineSegment(sketch, "E100", {"start": v(0, -40) * mm, "end": v(50, -40) * mm});
            skSolve(sketch);
        }
        {
            var Q0;
            {var subQ10=sQuery(id+"F22.wireOp",EDGE,"E99");Q0=makeQuery(id+"F22.imprint","IMPRINT",FACE,{"disambiguationData":[TD([[makeQuery(id+"F22.imprint","IMPRINT",EDGE,{"derivedFrom":subQ10}),-1.0]])]});}
            var Q1;
            {var subQ0=sQuery(id+"F22.wireOp",EDGE,"E97");var subQ1=sQuery(id+"F20.wireOp",EDGE,"E91");var subQ2=makeQuery(id+"F21.boolean.opBoolean","COPY",EDGE,{"derivedFrom":makeQuery(id+"F21.opExtrude","CAP_EDGE",EDGE,{"disambiguationData":[OSD([subQ1])],"isStart":true})});var subQ3=makeQuery(id+"F22.imprint","INTERSECT",VERTEX,{"derivedFrom":[subQ2,subQ0]});Q1=makeQuery(id+"F22.imprint","IMPRINT",FACE,{"disambiguationData":[TD([[makeQuery(id+"F22.imprint","IMPRINT",EDGE,{"disambiguationData":[TD([[subQ3,1.0]])],"derivedFrom":subQ0}),-1.0]])]});}
            extrude(context, id + "F23", {"entities" : qUnion([Q0, Q1]), "operationType" : NewBodyOperationType.REMOVE, "oppositeDirection" : true, "depth" : 2 * mm});
        }
        {
            var Q0;
            {var subQ10=sQuery(id+"F0.wireOp",EDGE,"E0.bottom");var subQ11=makeQuery(id+"F1.opExtrude","SWEPT_FACE",FACE,{"disambiguationData":[OSD([subQ10])]});var subQ12=sQuery(id+"F0.wireOp",EDGE,"E0.left");var subQ15=sQuery(id+"F0.wireOp",EDGE,"E0.right");var subQ21=sQuery(id+"F0.wireOp",EDGE,"E0.top");var subQ23=sQuery(id+"F0.wireOp",EDGE,"E1.left");var subQ25=sQuery(id+"F0.wireOp",EDGE,"E1.bottom");var subQ26=sQuery(id+"F0.wireOp",EDGE,"E1.top");var subQ27=sQuery(id+"F0.wireOp",EDGE,"E1.right");var subQ28=makeQuery(id+"F1.opExtrude","CAP_FACE",FACE,{"disambiguationData":[OSD([subQ10,subQ21,subQ12,subQ15,subQ25,subQ26,subQ23,subQ27])],"isStart":false});Q0=makeQuery(id+"F23.boolean.opBoolean","SPLIT",FACE,{"disambiguationData":[TD([subQ11])],"derivedFrom":makeQuery(id+"F21.boolean.opBoolean","SPLIT",FACE,{"disambiguationData":[TD([subQ11])],"derivedFrom":makeQuery(id+"F19.boolean.opBoolean","SPLIT",FACE,{"disambiguationData":[TD([subQ11])],"derivedFrom":makeQuery(id+"F17.boolean.opBoolean","SPLIT",FACE,{"disambiguationData":[TD([subQ11])],"derivedFrom":makeQuery(id+"F15.boolean.opBoolean","SPLIT",FACE,{"disambiguationData":[TD([subQ11])],"derivedFrom":makeQuery(id+"F13.boolean.opBoolean","SPLIT",FACE,{"disambiguationData":[TD([subQ11])],"derivedFrom":makeQuery(id+"F11.boolean.opBoolean","SPLIT",FACE,{"disambiguationData":[TD([subQ11])],"derivedFrom":makeQuery(id+"F9.boolean.opBoolean","SPLIT",FACE,{"disambiguationData":[TD([subQ11])],"derivedFrom":makeQuery(id+"F7.boolean.opBoolean","SPLIT",FACE,{"disambiguationData":[TD([subQ11])],"derivedFrom":makeQuery(id+"F5.boolean.opBoolean","SPLIT",FACE,{"disambiguationData":[TD([subQ11])],"derivedFrom":subQ28})})})})})})})})})});}
            var sketch = newSketch(context, id + "F24", { "sketchPlane" : qUnion([Q0])});
            skPoint(sketch, "E101", {"position": v(0, -40) * mm});
            skCircle(sketch, "E102", {"center": v(0, -40) * mm, "radius": 5 * mm});
            skLineSegment(sketch, "E103", {"start": v(-50, -40) * mm, "end": v(50, -39.68) * mm});
            skLineSegment(sketch, "E104", {"start": v(-50, -38.5) * mm, "end": v(50, -38.18) * mm});
            skLineSegment(sketch, "E105", {"start": v(-50, -41.5) * mm, "end": v(50, -41.18) * mm});
            skSolve(sketch);
        }
        {
            var Q0;
            {var subQ0=sQuery(id+"F24.wireOp",EDGE,"E102");var subQ1=sQuery(id+"F2.wireOp",EDGE,"E9");var subQ2=makeQuery(id+"F3.boolean.opBoolean","COPY",EDGE,{"derivedFrom":makeQuery(id+"F3.opExtrude","CAP_EDGE",EDGE,{"disambiguationData":[OSD([subQ1])],"isStart":true})});var subQ3=makeQuery(id+"F24.imprint","INTERSECT",VERTEX,{"derivedFrom":[subQ2,subQ0]});Q0=makeQuery(id+"F24.imprint","IMPRINT",FACE,{"disambiguationData":[TD([[makeQuery(id+"F24.imprint","IMPRINT",EDGE,{"disambiguationData":[TD([[subQ3,-1.0]])],"derivedFrom":subQ0}),-1.0]])]});}
            var Q1;
            {var subQ0=sQuery(id+"F24.wireOp",EDGE,"E103");var subQ1=sQuery(id+"F24.wireOp",EDGE,"E102");var subQ2=makeQuery(id+"F24.imprint","INTERSECT",VERTEX,{"disambiguationData":[OD(1.0)],"derivedFrom":[subQ1,subQ0]});Q1=makeQuery(id+"F24.imprint","IMPRINT",FACE,{"disambiguationData":[TD([[makeQuery(id+"F24.imprint","IMPRINT",EDGE,{"disambiguationData":[TD([[subQ2,-1.0]])],"derivedFrom":subQ1}),-1.0]])]});}
            var Q2;
            {var subQ0=sQuery(id+"F24.wireOp",EDGE,"E102");var subQ6=makeQuery(id+"F24.imprint","INTERSECT",VERTEX,{"derivedFrom":[makeQuery(id+"F23.boolean.opBoolean","COPY",EDGE,{"derivedFrom":makeQuery(id+"F23.opExtrude","CAP_EDGE",EDGE,{"disambiguationData":[OSD([sQuery(id+"F22.wireOp",EDGE,"E99")])],"isStart":true})}),subQ0]});Q2=makeQuery(id+"F24.imprint","IMPRINT",FACE,{"disambiguationData":[TD([[makeQuery(id+"F24.imprint","IMPRINT",EDGE,{"disambiguationData":[TD([[subQ6,1.0]])],"derivedFrom":subQ0}),1.0]])]});}
            var Q3;
            {var subQ0=sQuery(id+"F24.wireOp",EDGE,"E103");var subQ1=sQuery(id+"F24.wireOp",EDGE,"E102");var subQ2=makeQuery(id+"F24.imprint","INTERSECT",VERTEX,{"disambiguationData":[OD(1.0)],"derivedFrom":[subQ1,subQ0]});Q3=makeQuery(id+"F24.imprint","IMPRINT",FACE,{"disambiguationData":[TD([[makeQuery(id+"F24.imprint","IMPRINT",EDGE,{"disambiguationData":[TD([[subQ2,-1.0]])],"derivedFrom":subQ1}),1.0]])]});}
            var Q4;
            {var subQ0=sQuery(id+"F24.wireOp",EDGE,"E102");var subQ1=sQuery(id+"F22.wireOp",EDGE,"E99");var subQ2=makeQuery(id+"F23.boolean.opBoolean","COPY",EDGE,{"derivedFrom":makeQuery(id+"F23.opExtrude","CAP_EDGE",EDGE,{"disambiguationData":[OSD([subQ1])],"isStart":true})});var subQ3=makeQuery(id+"F24.imprint","INTERSECT",VERTEX,{"derivedFrom":[subQ2,subQ0]});Q4=makeQuery(id+"F24.imprint","IMPRINT",FACE,{"disambiguationData":[TD([[makeQuery(id+"F24.imprint","IMPRINT",EDGE,{"disambiguationData":[TD([[subQ3,1.0]])],"derivedFrom":subQ0}),-1.0]])]});}
            var Q5;
            {var subQ0=sQuery(id+"F24.wireOp",EDGE,"E103");var subQ1=sQuery(id+"F24.wireOp",EDGE,"E102");var subQ2=makeQuery(id+"F24.imprint","INTERSECT",VERTEX,{"disambiguationData":[OD(0.0)],"derivedFrom":[subQ1,subQ0]});Q5=makeQuery(id+"F24.imprint","IMPRINT",FACE,{"disambiguationData":[TD([[makeQuery(id+"F24.imprint","IMPRINT",EDGE,{"disambiguationData":[TD([[subQ2,1.0]])],"derivedFrom":subQ1}),-1.0]])]});}
            var Q6;
            {var subQ0=sQuery(id+"F24.wireOp",EDGE,"E102");var subQ1=makeQuery(id+"F3.boolean.opBoolean","COPY",EDGE,{"derivedFrom":makeQuery(id+"F3.opExtrude","CAP_EDGE",EDGE,{"disambiguationData":[OSD([sQuery(id+"F2.wireOp",EDGE,"E9")])],"isStart":true})});var subQ2=makeQuery(id+"F24.imprint","INTERSECT",VERTEX,{"derivedFrom":[subQ1,subQ0]});Q6=makeQuery(id+"F24.imprint","IMPRINT",FACE,{"disambiguationData":[TD([[makeQuery(id+"F24.imprint","IMPRINT",EDGE,{"disambiguationData":[TD([[subQ2,1.0]])],"derivedFrom":subQ0}),-1.0]])]});}
            var Q7;
            {var subQ0=sQuery(id+"F24.wireOp",EDGE,"E102");var subQ1=makeQuery(id+"F23.boolean.opBoolean","COPY",EDGE,{"derivedFrom":makeQuery(id+"F23.opExtrude","CAP_EDGE",EDGE,{"disambiguationData":[OSD([sQuery(id+"F22.wireOp",EDGE,"E99")])],"isStart":true})});var subQ2=makeQuery(id+"F24.imprint","INTERSECT",VERTEX,{"derivedFrom":[subQ1,subQ0]});Q7=makeQuery(id+"F24.imprint","IMPRINT",FACE,{"disambiguationData":[TD([[makeQuery(id+"F24.imprint","IMPRINT",EDGE,{"disambiguationData":[TD([[subQ2,-1.0]])],"derivedFrom":subQ0}),-1.0]])]});}
            extrude(context, id + "F25", {"entities" : qUnion([Q0, Q1, Q2, Q3, Q4, Q5, Q6, Q7]), "operationType" : NewBodyOperationType.REMOVE, "oppositeDirection" : true, "depth" : 2 * mm});
        }
        {
            var Q0;
            {var subQ0=sQuery(id+"F0.wireOp",EDGE,"E0.bottom");var subQ1=makeQuery(id+"F1.opExtrude","SWEPT_FACE",FACE,{"disambiguationData":[OSD([subQ0])]});var subQ2=sQuery(id+"F0.wireOp",EDGE,"E0.right");var subQ4=sQuery(id+"F0.wireOp",EDGE,"E0.left");var subQ21=sQuery(id+"F0.wireOp",EDGE,"E0.top");var subQ23=sQuery(id+"F0.wireOp",EDGE,"E1.left");var subQ25=sQuery(id+"F0.wireOp",EDGE,"E1.bottom");var subQ26=sQuery(id+"F0.wireOp",EDGE,"E1.top");var subQ27=sQuery(id+"F0.wireOp",EDGE,"E1.right");var subQ28=makeQuery(id+"F1.opExtrude","CAP_FACE",FACE,{"disambiguationData":[OSD([subQ0,subQ21,subQ4,subQ2,subQ25,subQ26,subQ23,subQ27])],"isStart":false});Q0=makeQuery(id+"F25.boolean.opBoolean","SPLIT",FACE,{"disambiguationData":[TD([subQ1])],"derivedFrom":makeQuery(id+"F23.boolean.opBoolean","SPLIT",FACE,{"disambiguationData":[TD([subQ1])],"derivedFrom":makeQuery(id+"F21.boolean.opBoolean","SPLIT",FACE,{"disambiguationData":[TD([subQ1])],"derivedFrom":makeQuery(id+"F19.boolean.opBoolean","SPLIT",FACE,{"disambiguationData":[TD([subQ1])],"derivedFrom":makeQuery(id+"F17.boolean.opBoolean","SPLIT",FACE,{"disambiguationData":[TD([subQ1])],"derivedFrom":makeQuery(id+"F15.boolean.opBoolean","SPLIT",FACE,{"disambiguationData":[TD([subQ1])],"derivedFrom":makeQuery(id+"F13.boolean.opBoolean","SPLIT",FACE,{"disambiguationData":[TD([subQ1])],"derivedFrom":makeQuery(id+"F11.boolean.opBoolean","SPLIT",FACE,{"disambiguationData":[TD([subQ1])],"derivedFrom":makeQuery(id+"F9.boolean.opBoolean","SPLIT",FACE,{"disambiguationData":[TD([subQ1])],"derivedFrom":makeQuery(id+"F7.boolean.opBoolean","SPLIT",FACE,{"disambiguationData":[TD([subQ1])],"derivedFrom":makeQuery(id+"F5.boolean.opBoolean","SPLIT",FACE,{"disambiguationData":[TD([subQ1])],"derivedFrom":subQ28})})})})})})})})})})});}
            var sketch = newSketch(context, id + "F26", { "sketchPlane" : qUnion([Q0])});
            skText(sketch, "E106", { "text": "S", "fontName": "OpenSans-Regular.ttf"});
            const initialGuessF26  = {"E106": [-0.002, -0.0495, 1, 0, 0.00764]};
            skSetInitialGuess(sketch, initialGuessF26);
            skSolve(sketch);
        }
        {
            var Q0;
            Q0=qSketchRegion(id+"F26",true);
            extrude(context, id + "F27", {"entities" : qUnion([Q0]), "operationType" : NewBodyOperationType.ADD, "depth" : 1.5 * mm});
        }
    });
